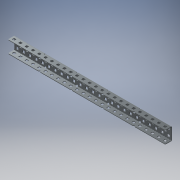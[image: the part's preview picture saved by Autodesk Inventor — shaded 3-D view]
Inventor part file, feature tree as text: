
AUTODESK INVENTOR PART (.ipt)
format: ipt  version: 2018 (Build 220112000, 112)  size: 2,717,184 bytes
history: native  units: mm (DEFAULTED — no unit token found)
features: other x124, extrude x124, pattern_linear x3, sketch x2, imported_body x1, plane x1, mirror x1
ambient origin geometry x8: Origin, YZ Plane, XZ Plane, XY Plane, X Axis, Y Axis, Z Axis, Center Point
bodies: Solid1 (feature_tree)
feature tree (256):
  imported_body  "Base1"
  sketch  "Sketch1"  dims[d1=1.1684mm]
  pattern_linear  "Rectangular Pattern1"  Spacing1=1.1684mm  [1 undecoded]
  pattern_linear  "Rectangular Pattern2"  Spacing1=0.0mm  [1 undecoded]
  pattern_linear  "Rectangular Pattern3"  Count1=25  [1 undecoded]
  plane  "Work Plane1"
  mirror  "Mirror1"
  other  "Srf1"
  other  "Srf2"
  other  "Srf3"
  other  "Srf4"
  other  "Srf5"
  other  "Srf6"
  other  "Srf7"
  other  "Srf8"
  other  "Srf9"
  other  "Srf10"
  other  "Srf11"
  other  "Srf12"
  other  "Srf13"
  other  "Srf14"
  other  "Srf15"
  other  "Srf16"
  other  "Srf17"
  other  "Srf18"
  other  "Srf19"
  other  "Srf20"
  other  "Srf21"
  other  "Srf22"
  other  "Srf23"
  other  "Srf24"
  other  "Srf25"
  other  "Srf26"
  other  "Srf27"
  other  "Srf28"
  other  "Srf29"
  other  "Srf30"
  other  "Srf31"
  other  "Srf32"
  other  "Srf33"
  other  "Srf34"
  other  "Srf35"
  other  "Srf36"
  other  "Srf37"
  other  "Srf38"
  other  "Srf39"
  other  "Srf40"
  other  "Srf41"
  other  "Srf42"
  other  "Srf43"
  other  "Srf44"
  other  "Srf45"
  other  "Srf46"
  other  "Srf47"
  other  "Srf48"
  other  "Srf49"
  other  "Srf50"
  other  "Srf51"
  other  "Srf52"
  other  "Srf53"
  other  "Srf54"
  other  "Srf55"
  other  "Srf56"
  other  "Srf57"
  other  "Srf58"
  other  "Srf59"
  other  "Srf60"
  other  "Srf61"
  other  "Srf62"
  other  "Srf63"
  other  "Srf64"
  other  "Srf65"
  other  "Srf66"
  other  "Srf67"
  other  "Srf68"
  other  "Srf69"
  other  "Srf70"
  other  "Srf71"
  other  "Srf72"
  other  "Srf73"
  other  "Srf74"
  sketch  "Sketch2"  dims[d2=0.0mm d3=1.1684mm d4=0.0mm d5=250.0mm d7=12.7mm d8=20.0mm d10=12.7mm d11=240.0mm d13=12.7mm d14=1.1684mm d15=0.0mm d16=250.0mm d18=12.7mm d19=0.0mm d20=0.0mm d21=0.0mm d22=0.0mm d23=0.0mm d24=0.0mm d25=0.0mm d26=0.0mm d27=0.0mm d28=0.0mm d29=0.0mm d30=0.0mm d31=0.0mm d32=0.0mm d33=0.0mm d34=0.0mm d35=0.0mm d36=0.0mm d37=0.0mm d38=0.0mm d39=0.0mm d40=0.0mm d41=0.0mm d42=0.0mm d43=0.0mm d44=0.0mm d45=0.0mm d46=0.0mm d47=0.0mm d48=0.0mm d49=0.0mm d50=0.0mm d51=0.0mm d52=0.0mm d53=0.0mm d54=0.0mm d55=0.0mm d56=0.0mm d57=0.0mm d58=0.0mm d59=0.0mm d60=0.0mm d61=0.0mm d62=0.0mm d63=0.0mm d64=0.0mm d65=0.0mm d66=0.0mm d67=0.0mm d68=0.0mm d69=0.0mm d70=0.0mm d71=0.0mm d72=0.0mm d73=0.0mm d74=0.0mm d75=0.0mm d76=0.0mm d77=0.0mm d78=0.0mm d79=0.0mm d80=0.0mm d81=0.0mm d82=0.0mm d83=0.0mm d84=0.0mm d85=0.0mm d86=0.0mm d87=0.0mm d88=0.0mm d89=0.0mm d90=0.0mm d91=0.0mm d92=0.0mm d93=0.0mm d94=0.0mm d95=0.0mm d96=0.0mm d97=0.0mm d98=0.0mm d99=0.0mm d100=0.0mm d101=0.0mm d102=0.0mm d103=0.0mm d104=0.0mm d105=0.0mm d106=0.0mm d107=0.0mm d108=0.0mm d109=0.0mm d110=0.0mm d111=0.0mm d112=0.0mm d113=0.0mm d114=0.0mm d115=0.0mm d116=0.0mm d117=0.0mm d118=0.0mm d119=0.0mm d120=0.0mm d121=0.0mm d122=0.0mm d123=0.0mm d124=0.0mm d125=0.0mm d126=0.0mm d127=0.0mm d128=0.0mm d129=0.0mm d130=0.0mm d131=0.0mm d132=0.0mm d133=0.0mm d134=0.0mm d135=0.0mm d136=0.0mm d137=0.0mm d138=0.0mm d139=0.0mm d140=0.0mm d141=0.0mm d142=0.0mm d143=0.0mm d144=0.0mm d145=0.0mm d146=0.0mm d147=0.0mm d148=0.0mm d149=0.0mm d150=0.0mm d151=0.0mm d152=0.0mm d153=0.0mm d154=0.0mm d155=0.0mm d156=0.0mm d157=0.0mm d158=0.0mm d159=0.0mm d160=0.0mm d161=0.0mm d162=0.0mm d163=0.0mm d164=0.0mm d165=0.0mm d166=0.0mm d167=0.0mm d168=0.0mm d169=0.0mm d170=0.0mm d171=0.0mm d172=0.0mm d173=0.0mm d174=0.0mm d175=0.0mm d176=0.0mm d177=0.0mm d178=0.0mm d179=0.0mm d180=0.0mm d181=0.0mm d182=0.0mm d183=0.0mm d184=0.0mm d185=0.0mm d186=0.0mm d187=0.0mm d188=0.0mm d189=0.0mm d190=0.0mm d191=0.0mm d192=0.0mm d193=0.0mm d194=0.0mm d195=0.0mm d196=0.0mm d197=0.0mm d198=0.0mm d199=0.0mm d200=0.0mm d201=0.0mm d202=0.0mm d203=0.0mm d204=0.0mm d205=0.0mm d206=0.0mm d207=0.0mm d208=0.0mm d209=0.0mm d210=0.0mm d211=0.0mm d212=0.0mm d213=0.0mm d214=0.0mm d215=0.0mm d216=0.0mm d217=0.0mm d218=0.0mm d219=0.0mm d220=0.0mm d221=0.0mm d222=0.0mm d223=0.0mm d224=0.0mm d225=0.0mm d226=0.0mm d227=0.0mm d228=0.0mm d229=0.0mm d230=0.0mm d231=0.0mm d232=0.0mm d233=0.0mm d234=0.0mm d235=0.0mm d236=0.0mm d237=0.0mm d238=0.0mm d239=0.0mm d240=0.0mm d241=0.0mm d242=0.0mm d243=0.0mm d244=0.0mm d245=0.0mm d246=0.0mm d247=0.0mm d248=0.0mm d249=0.0mm d250=0.0mm d251=0.0mm d252=0.0mm d253=0.0mm d254=0.0mm d255=0.0mm d256=0.0mm d257=0.0mm d258=0.0mm d259=0.0mm d260=0.0mm d261=0.0mm d262=0.0mm d263=0.0mm]
  other  "Srf75"
  other  "Srf76"
  other  "Srf77"
  other  "Srf78"
  other  "Srf79"
  other  "Srf80"
  other  "Srf81"
  other  "Srf82"
  other  "Srf83"
  other  "Srf84"
  other  "Srf85"
  other  "Srf86"
  other  "Srf87"
  other  "Srf88"
  other  "Srf89"
  other  "Srf90"
  other  "Srf91"
  other  "Srf92"
  other  "Srf93"
  other  "Srf94"
  other  "Srf95"
  other  "Srf96"
  other  "Srf97"
  other  "Srf98"
  other  "Srf99"
  other  "Srf100"
  other  "Srf101"
  other  "Srf102"
  other  "Srf103"
  other  "Srf104"
  other  "Srf105"
  other  "Srf106"
  other  "Srf107"
  other  "Srf108"
  other  "Srf109"
  other  "Srf110"
  other  "Srf111"
  other  "Srf112"
  other  "Srf113"
  other  "Srf114"
  other  "Srf115"
  other  "Srf116"
  other  "Srf117"
  other  "Srf118"
  other  "Srf119"
  other  "Srf120"
  other  "Srf121"
  other  "Srf122"
  other  "Srf123"
  other  "Srf124"
  extrude  "ExtrusionSrf1"  Depth=12.7mm
  extrude  "ExtrusionSrf2"  Depth=20.0mm
  extrude  "ExtrusionSrf75"  Depth=240.0mm
  extrude  "ExtrusionSrf3"  Depth=12.7mm
  extrude  "ExtrusionSrf4"  Depth=1.1684mm
  extrude  "ExtrusionSrf5"  TaperAngle=0.0deg  [1 undecoded]
  extrude  "ExtrusionSrf6"  Depth=250.0mm
  extrude  "ExtrusionSrf7"  Depth=12.7mm
  extrude  "ExtrusionSrf8"  TaperAngle=0.0deg  [1 undecoded]
  extrude  "ExtrusionSrf9"  TaperAngle=0.0deg  [1 undecoded]
  extrude  "ExtrusionSrf10"  TaperAngle=0.0deg  [1 undecoded]
  extrude  "ExtrusionSrf11"  TaperAngle=0.0deg  [1 undecoded]
  extrude  "ExtrusionSrf12"  TaperAngle=0.0deg  [1 undecoded]
  extrude  "ExtrusionSrf13"  TaperAngle=0.0deg  [1 undecoded]
  extrude  "ExtrusionSrf14"  TaperAngle=0.0deg  [1 undecoded]
  extrude  "ExtrusionSrf15"  TaperAngle=0.0deg  [1 undecoded]
  extrude  "ExtrusionSrf16"  TaperAngle=0.0deg  [1 undecoded]
  extrude  "ExtrusionSrf17"  TaperAngle=0.0deg  [1 undecoded]
  extrude  "ExtrusionSrf18"  TaperAngle=0.0deg  [1 undecoded]
  extrude  "ExtrusionSrf19"  TaperAngle=0.0deg  [1 undecoded]
  extrude  "ExtrusionSrf20"  TaperAngle=0.0deg  [1 undecoded]
  extrude  "ExtrusionSrf21"  TaperAngle=0.0deg  [1 undecoded]
  extrude  "ExtrusionSrf22"  TaperAngle=0.0deg  [1 undecoded]
  extrude  "ExtrusionSrf23"  TaperAngle=0.0deg  [1 undecoded]
  extrude  "ExtrusionSrf24"  TaperAngle=0.0deg  [1 undecoded]
  extrude  "ExtrusionSrf25"  TaperAngle=0.0deg  [1 undecoded]
  extrude  "ExtrusionSrf26"  TaperAngle=0.0deg  [1 undecoded]
  extrude  "ExtrusionSrf27"  TaperAngle=0.0deg  [1 undecoded]
  extrude  "ExtrusionSrf28"  TaperAngle=0.0deg  [1 undecoded]
  extrude  "ExtrusionSrf29"  TaperAngle=0.0deg  [1 undecoded]
  extrude  "ExtrusionSrf30"  TaperAngle=0.0deg  [1 undecoded]
  extrude  "ExtrusionSrf31"  TaperAngle=0.0deg  [1 undecoded]
  extrude  "ExtrusionSrf32"  TaperAngle=0.0deg  [1 undecoded]
  extrude  "ExtrusionSrf33"  TaperAngle=0.0deg  [1 undecoded]
  extrude  "ExtrusionSrf34"  TaperAngle=0.0deg  [1 undecoded]
  extrude  "ExtrusionSrf35"  TaperAngle=0.0deg  [1 undecoded]
  extrude  "ExtrusionSrf36"  TaperAngle=0.0deg  [1 undecoded]
  extrude  "ExtrusionSrf37"  TaperAngle=0.0deg  [1 undecoded]
  extrude  "ExtrusionSrf38"  TaperAngle=0.0deg  [1 undecoded]
  extrude  "ExtrusionSrf39"  TaperAngle=0.0deg  [1 undecoded]
  extrude  "ExtrusionSrf40"  TaperAngle=0.0deg  [1 undecoded]
  extrude  "ExtrusionSrf41"  TaperAngle=0.0deg  [1 undecoded]
  extrude  "ExtrusionSrf42"  TaperAngle=0.0deg  [1 undecoded]
  extrude  "ExtrusionSrf43"  TaperAngle=0.0deg  [1 undecoded]
  extrude  "ExtrusionSrf44"  TaperAngle=0.0deg  [1 undecoded]
  extrude  "ExtrusionSrf45"  TaperAngle=0.0deg  [1 undecoded]
  extrude  "ExtrusionSrf46"  TaperAngle=0.0deg  [1 undecoded]
  extrude  "ExtrusionSrf47"  TaperAngle=0.0deg  [1 undecoded]
  extrude  "ExtrusionSrf48"  TaperAngle=0.0deg  [1 undecoded]
  extrude  "ExtrusionSrf49"  TaperAngle=0.0deg  [1 undecoded]
  extrude  "ExtrusionSrf50"  TaperAngle=0.0deg  [1 undecoded]
  extrude  "ExtrusionSrf51"  TaperAngle=0.0deg  [1 undecoded]
  extrude  "ExtrusionSrf52"  TaperAngle=0.0deg  [1 undecoded]
  extrude  "ExtrusionSrf53"  TaperAngle=0.0deg  [1 undecoded]
  extrude  "ExtrusionSrf54"  TaperAngle=0.0deg  [1 undecoded]
  extrude  "ExtrusionSrf55"  TaperAngle=0.0deg  [1 undecoded]
  extrude  "ExtrusionSrf56"  TaperAngle=0.0deg  [1 undecoded]
  extrude  "ExtrusionSrf57"  TaperAngle=0.0deg  [1 undecoded]
  extrude  "ExtrusionSrf58"  TaperAngle=0.0deg  [1 undecoded]
  extrude  "ExtrusionSrf59"  TaperAngle=0.0deg  [1 undecoded]
  extrude  "ExtrusionSrf60"  TaperAngle=0.0deg  [1 undecoded]
  extrude  "ExtrusionSrf61"  TaperAngle=0.0deg  [1 undecoded]
  extrude  "ExtrusionSrf62"  TaperAngle=0.0deg  [1 undecoded]
  extrude  "ExtrusionSrf63"  TaperAngle=0.0deg  [1 undecoded]
  extrude  "ExtrusionSrf64"  TaperAngle=0.0deg  [1 undecoded]
  extrude  "ExtrusionSrf65"  TaperAngle=0.0deg  [1 undecoded]
  extrude  "ExtrusionSrf66"  TaperAngle=0.0deg  [1 undecoded]
  extrude  "ExtrusionSrf67"  TaperAngle=0.0deg  [1 undecoded]
  extrude  "ExtrusionSrf68"  TaperAngle=0.0deg  [1 undecoded]
  extrude  "ExtrusionSrf69"  TaperAngle=0.0deg  [1 undecoded]
  extrude  "ExtrusionSrf70"  TaperAngle=0.0deg  [1 undecoded]
  extrude  "ExtrusionSrf71"  TaperAngle=0.0deg  [1 undecoded]
  extrude  "ExtrusionSrf72"  TaperAngle=0.0deg  [1 undecoded]
  extrude  "ExtrusionSrf73"  TaperAngle=0.0deg  [1 undecoded]
  extrude  "ExtrusionSrf74"  TaperAngle=0.0deg  [1 undecoded]
  extrude  "ExtrusionSrf76"  TaperAngle=0.0deg  [1 undecoded]
  extrude  "ExtrusionSrf77"  TaperAngle=0.0deg  [1 undecoded]
  extrude  "ExtrusionSrf78"  TaperAngle=0.0deg  [1 undecoded]
  extrude  "ExtrusionSrf79"  TaperAngle=0.0deg  [1 undecoded]
  extrude  "ExtrusionSrf80"  TaperAngle=0.0deg  [1 undecoded]
  extrude  "ExtrusionSrf81"  TaperAngle=0.0deg  [1 undecoded]
  extrude  "ExtrusionSrf82"  TaperAngle=0.0deg  [1 undecoded]
  extrude  "ExtrusionSrf83"  TaperAngle=0.0deg  [1 undecoded]
  extrude  "ExtrusionSrf84"  TaperAngle=0.0deg  [1 undecoded]
  extrude  "ExtrusionSrf85"  TaperAngle=0.0deg  [1 undecoded]
  extrude  "ExtrusionSrf86"  TaperAngle=0.0deg  [1 undecoded]
  extrude  "ExtrusionSrf87"  TaperAngle=0.0deg  [1 undecoded]
  extrude  "ExtrusionSrf88"  TaperAngle=0.0deg  [1 undecoded]
  extrude  "ExtrusionSrf89"  TaperAngle=0.0deg  [1 undecoded]
  extrude  "ExtrusionSrf90"  TaperAngle=0.0deg  [1 undecoded]
  extrude  "ExtrusionSrf91"  TaperAngle=0.0deg  [1 undecoded]
  extrude  "ExtrusionSrf92"  TaperAngle=0.0deg  [1 undecoded]
  extrude  "ExtrusionSrf93"  TaperAngle=0.0deg  [1 undecoded]
  extrude  "ExtrusionSrf94"  TaperAngle=0.0deg  [1 undecoded]
  extrude  "ExtrusionSrf95"  TaperAngle=0.0deg  [1 undecoded]
  extrude  "ExtrusionSrf96"  TaperAngle=0.0deg  [1 undecoded]
  extrude  "ExtrusionSrf97"  TaperAngle=0.0deg  [1 undecoded]
  extrude  "ExtrusionSrf98"  TaperAngle=0.0deg  [1 undecoded]
  extrude  "ExtrusionSrf99"  TaperAngle=0.0deg  [1 undecoded]
  extrude  "ExtrusionSrf100"  TaperAngle=0.0deg  [1 undecoded]
  extrude  "ExtrusionSrf101"  TaperAngle=0.0deg  [1 undecoded]
  extrude  "ExtrusionSrf102"  TaperAngle=0.0deg  [1 undecoded]
  extrude  "ExtrusionSrf103"  TaperAngle=0.0deg  [1 undecoded]
  extrude  "ExtrusionSrf104"  TaperAngle=0.0deg  [1 undecoded]
  extrude  "ExtrusionSrf105"  TaperAngle=0.0deg  [1 undecoded]
  extrude  "ExtrusionSrf106"  TaperAngle=0.0deg  [1 undecoded]
  extrude  "ExtrusionSrf107"  TaperAngle=0.0deg  [1 undecoded]
  extrude  "ExtrusionSrf108"  TaperAngle=0.0deg  [1 undecoded]
  extrude  "ExtrusionSrf109"  TaperAngle=0.0deg  [1 undecoded]
  extrude  "ExtrusionSrf110"  TaperAngle=0.0deg  [1 undecoded]
  extrude  "ExtrusionSrf111"  TaperAngle=0.0deg  [1 undecoded]
  extrude  "ExtrusionSrf112"  TaperAngle=0.0deg  [1 undecoded]
  extrude  "ExtrusionSrf113"  TaperAngle=0.0deg  [1 undecoded]
  extrude  "ExtrusionSrf114"  TaperAngle=0.0deg  [1 undecoded]
  extrude  "ExtrusionSrf115"  TaperAngle=0.0deg  [1 undecoded]
  extrude  "ExtrusionSrf116"  TaperAngle=0.0deg  [1 undecoded]
  extrude  "ExtrusionSrf117"  TaperAngle=0.0deg  [1 undecoded]
  extrude  "ExtrusionSrf118"  TaperAngle=0.0deg  [1 undecoded]
  extrude  "ExtrusionSrf119"  TaperAngle=0.0deg  [1 undecoded]
  extrude  "ExtrusionSrf120"  TaperAngle=0.0deg  [1 undecoded]
  extrude  "ExtrusionSrf121"  TaperAngle=0.0deg  [1 undecoded]
  extrude  "ExtrusionSrf122"  TaperAngle=0.0deg  [1 undecoded]
  extrude  "ExtrusionSrf123"  TaperAngle=0.0deg  [1 undecoded]
  extrude  "ExtrusionSrf124"  TaperAngle=0.0deg  [1 undecoded]
note: 120 required parameter values undecoded (feature->parameter linkage not recoverable at this tier; creation-order binding heuristic only, values carry confidence <= 0.55)
